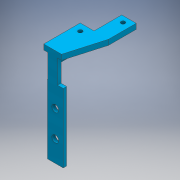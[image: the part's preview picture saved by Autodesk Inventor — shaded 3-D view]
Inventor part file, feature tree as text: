
AUTODESK INVENTOR PART (.ipt)
format: ipt  version: 2018.3 (Build 223284000, 284)  size: 1,038,848 bytes
history: native  units: mm
features: extrude x95, sketch x95, other x2
ambient origin geometry x8: Origin, YZ Plane, XZ Plane, XY Plane, X Axis, Y Axis, Z Axis, Center Point
bodies: Body1 (feature_tree), Body2 (feature_tree)
feature tree (192):
  other  "Sólido1"
  extrude  "Extrusión1"  Depth=10.0mm TaperAngle=0.0deg
  extrude  "Extrusión2"  Depth=33.0mm TaperAngle=0.0deg
  extrude  "Extrusión3"  Depth=29.0mm TaperAngle=0.0deg
  extrude  "Extrusión4"  Depth=21.0mm
  extrude  "Extrusión5"  Depth=4.0mm TaperAngle=0.0deg
  extrude  "Extrusión6"  Depth=37.0mm TaperAngle=0.0deg
  extrude  "Extrusión7"  Depth=94.0mm TaperAngle=0.0deg
  extrude  "Extrusión8"  Depth=15.0mm
  extrude  "Extrusión9"  Depth=64.0mm TaperAngle=0.0deg
  extrude  "Extrusión10"  Depth=10.0mm
  extrude  "Extrusión11"  Depth=64.0mm TaperAngle=0.0deg
  extrude  "Extrusión13"  Depth=10.0mm
  extrude  "Extrusión14"  Depth=10.0mm
  extrude  "Extrusión15"  Depth=19.0mm TaperAngle=0.0deg
  extrude  "Extrusión17"  Depth=19.0mm TaperAngle=0.0deg
  extrude  "Extrusión18"  Depth=15.0mm TaperAngle=0.0deg
  extrude  "Extrusión19"  Depth=3.0mm
  extrude  "Extrusión20"  Depth=6.0mm TaperAngle=0.0deg
  extrude  "Extrusión21"  Depth=10.0mm TaperAngle=0.0deg
  extrude  "Extrusión22"  Depth=10.0mm TaperAngle=0.0deg
  extrude  "Extrusión23"  Depth=10.0mm TaperAngle=0.0deg
  extrude  "Extrusión27"  Depth=15.0mm
  extrude  "Extrusión28"  Depth=5.0mm
  extrude  "Extrusión29"  Depth=4.0mm TaperAngle=0.0deg
  extrude  "Extrusión30"  Depth=24.5mm TaperAngle=0.0deg
  extrude  "Extrusión31"  Depth=24.5mm TaperAngle=0.0deg
  extrude  "Extrusión32"  Depth=4.3mm
  extrude  "Extrusión33"  Depth=3.7mm
  sketch  "Boceto34"  dims[d152=3.7mm d153=3.7mm]
  extrude  "Extrusión35"  Depth=3.7mm
  extrude  "Extrusión36"  Depth=25.5mm TaperAngle=0.0deg
  extrude  "Extrusión38"  Depth=5.2mm
  extrude  "Extrusión39"  Depth=5.2mm
  extrude  "Extrusión40"  Depth=45.25mm TaperAngle=0.0deg
  extrude  "Extrusión41"  Depth=71.0mm TaperAngle=0.0deg
  extrude  "Extrusión42"  Depth=1.7mm TaperAngle=0.0deg
  extrude  "Extrusión43"  Depth=33.0mm
  extrude  "Extrusión44"  Depth=2.4mm TaperAngle=0.0deg
  extrude  "Extrusión45"  Depth=85.9mm TaperAngle=0.0deg
  extrude  "Extrusión46"  Depth=2.973mm
  extrude  "Extrusión47"  Depth=3.7mm
  extrude  "Extrusión48"  Depth=3.7mm
  extrude  "Extrusión49"  Depth=5.0mm TaperAngle=0.0deg
  extrude  "Extrusión50"  Depth=0.534mm
  extrude  "Extrusión53"  Depth=2.384mm TaperAngle=0.0deg
  extrude  "Extrusión54"  Depth=5.884mm TaperAngle=0.0deg
  extrude  "Extrusión55"  Depth=14.25mm TaperAngle=0.0deg
  extrude  "Extrusión56"  Depth=11.0mm TaperAngle=0.0deg
  extrude  "Extrusión57"  Depth=3.1mm
  sketch  "Boceto57"  dims[d235=11.0mm d236=0.0mm d237=11.0mm]
  extrude  "Extrusión58"  Depth=11.0mm
  extrude  "Extrusión59"  Depth=11.0mm TaperAngle=0.0deg
  extrude  "Extrusión60"  Depth=13.0mm TaperAngle=0.0deg
  extrude  "Extrusión61"  Depth=14.0mm TaperAngle=0.0deg
  extrude  "Extrusión62"  Depth=4.3mm
  extrude  "Extrusión63"  Depth=5.0mm TaperAngle=0.0deg
  extrude  "Extrusión64"  Depth=21.5mm TaperAngle=0.0deg
  extrude  "Extrusión65"  Depth=8.0mm TaperAngle=0.0deg
  extrude  "Extrusión66"  Depth=8.0mm TaperAngle=0.0deg
  extrude  "Extrusión67"  Depth=4.0mm TaperAngle=0.0deg
  extrude  "Extrusión68"  Depth=8.0mm TaperAngle=0.0deg
  extrude  "Extrusión69"  Depth=4.0mm TaperAngle=0.0deg
  extrude  "Extrusión74"  Depth=4.3mm TaperAngle=0.0deg
  extrude  "Extrusión75"  Depth=15.0mm TaperAngle=0.0deg
  extrude  "Extrusión76"  Depth=15.0mm TaperAngle=0.0deg
  extrude  "Extrusión77"  Depth=15.0mm TaperAngle=0.0deg
  extrude  "Extrusión78"  Depth=79.25mm TaperAngle=0.0deg
  extrude  "Extrusión79"  Depth=5.0mm TaperAngle=0.0deg
  extrude  "Extrusión80"  Depth=4.0mm TaperAngle=0.0deg
  extrude  "Extrusión81"  Depth=3.0mm
  extrude  "Extrusión82"  Depth=2.53mm TaperAngle=0.0deg
  extrude  "Extrusión83"  Depth=4.0mm TaperAngle=0.0deg
  extrude  "Extrusión84"  Depth=2.6mm TaperAngle=0.0deg
  extrude  "Extrusión85"  Depth=5.2mm TaperAngle=0.0deg
  extrude  "Extrusión86"  Depth=46.25mm TaperAngle=0.0deg
  extrude  "Extrusión87"  [1 undecoded]
  extrude  "Extrusión88"  [1 undecoded]
  extrude  "Extrusión89"  [1 undecoded]
  extrude  "Extrusión90"  [1 undecoded]
  extrude  "Extrusión91"  [1 undecoded]
  extrude  "Extrusión92"  [1 undecoded]
  extrude  "Extrusión93"  [1 undecoded]
  extrude  "Extrusión94"  [1 undecoded]
  extrude  "Extrusión95"  [1 undecoded]
  extrude  "Extrusión96"  [1 undecoded]
  extrude  "Extrusión97"  [1 undecoded]
  extrude  "Extrusión98"  [1 undecoded]
  extrude  "Extrusión99"  [1 undecoded]
  extrude  "Extrusión100"  [1 undecoded]
  extrude  "Extrusión101"  [1 undecoded]
  extrude  "Extrusión102"  [1 undecoded]
  extrude  "Extrusión103"  [1 undecoded]
  extrude  "Extrusión104"  [1 undecoded]
  extrude  "Extrusión105"  [1 undecoded]
  extrude  "Extrusión106"  [1 undecoded]
  extrude  "Extrusión107"  [1 undecoded]
  extrude  "Extrusión108"  [1 undecoded]
  sketch  "Boceto1"  dims[d0=18.0mm d1=0.0mm d2=10.0mm d3=0.0mm]
  sketch  "Boceto2"  dims[d6=3.0mm d7=33.0mm d8=0.0mm]
  sketch  "Boceto4"  dims[d9=35.0mm d10=29.0mm d11=0.0mm]
  sketch  "Boceto5"  dims[d12=2.0mm d13=21.0mm]
  sketch  "Boceto6"  dims[d14=20.0mm d15=4.0mm d16=0.0mm]
  sketch  "Boceto7"  dims[d17=8.0mm d18=0.0mm d19=37.0mm d20=0.0mm]
  sketch  "Boceto8"  dims[d21=2.0mm d22=94.0mm d23=0.0mm]
  sketch  "Boceto9"  dims[d30=5.0mm d31=15.0mm]
  sketch  "Boceto12"  dims[d32=15.0mm d33=64.0mm d34=0.0mm]
  sketch  "Boceto13"  dims[d35=64.0mm d36=0.0mm d38=10.0mm]
  sketch  "Boceto15"  dims[d40=15.0mm d41=64.0mm d42=0.0mm]
  sketch  "Boceto17"  dims[d48=46.25mm d49=10.0mm]
  sketch  "Boceto18"  dims[d50=23.0mm d51=0.0mm d52=10.0mm]
  sketch  "Boceto19"  dims[d53=19.0mm d54=0.0mm d58=19.0mm d59=0.0mm]
  sketch  "Boceto20"  dims[d68=19.0mm d69=0.0mm d70=19.0mm d71=0.0mm]
  sketch  "Boceto21"  dims[d73=19.0mm d74=0.0mm d76=15.0mm d77=0.0mm]
  sketch  "Boceto22"  dims[d78=4.0mm d79=0.0mm d80=3.0mm]
  sketch  "Boceto23"  dims[d81=6.0mm d82=0.0mm d87=6.0mm d88=0.0mm]
  sketch  "Boceto24"  dims[d89=4.0mm d96=10.0mm d97=0.0mm]
  sketch  "Boceto25"  dims[d101=10.0mm d102=0.0mm d104=10.0mm d105=0.0mm]
  sketch  "Boceto26"  dims[d106=2.0mm d107=10.0mm d108=0.0mm]
  sketch  "Boceto27"  dims[d110=11.0mm d111=15.0mm]
  sketch  "Boceto28"  dims[d112=10.0mm d113=0.0mm d114=5.0mm]
  sketch  "Boceto29"  dims[d115=23.0mm d116=0.0mm d117=4.0mm d118=0.0mm]
  sketch  "Boceto30"  dims[d124=24.5mm d125=0.0mm d132=24.5mm d133=0.0mm]
  sketch  "Boceto31"  dims[d141=24.5mm d142=0.0mm d145=24.5mm d146=0.0mm]
  sketch  "Boceto32"  dims[d147=10.0mm d148=0.0mm d149=4.3mm]
  sketch  "Boceto33"  dims[d150=4.3mm d151=3.7mm]
  sketch  "Boceto35"  dims[d154=3.7mm d155=25.5mm d156=0.0mm]
  sketch  "Boceto37"  dims[d157=5.2mm d158=5.2mm]
  sketch  "Boceto38"  dims[d159=25.5mm d160=0.0mm d161=5.2mm]
  sketch  "Boceto39"  dims[d162=5.2mm d163=45.25mm d164=0.0mm]
  sketch  "Boceto40"  dims[d165=2.6mm d166=71.0mm d167=0.0mm]
  sketch  "Boceto41"  dims[d168=10.005mm d169=1.7mm d170=0.0mm]
  sketch  "Boceto42"  dims[d171=33.0mm d172=33.0mm]
  sketch  "Boceto43"  dims[d173=38.28mm d174=4.0mm d175=0.0mm d176=0.0mm d178=2.4mm d179=0.0mm]
  sketch  "Boceto44"  dims[d180=6.15mm d181=0.0mm d184=85.9mm d185=0.0mm]
  sketch  "Boceto45"  dims[d186=2.973mm d187=2.973mm]
  sketch  "Boceto46"  dims[d188=5.0mm d189=0.0mm d205=3.7mm]
  sketch  "Boceto47"  dims[d209=3.7mm d210=3.7mm]
  sketch  "Boceto48"  dims[d211=3.7mm d212=5.0mm d213=0.0mm]
  sketch  "Boceto49"  dims[d214=5.0mm d215=0.0mm d216=0.534mm]
  sketch  "Boceto50"  dims[d217=5.0mm d218=0.0mm d219=2.384mm d220=0.0mm]
  sketch  "Boceto53"  dims[d221=17.6mm d222=5.884mm d223=0.0mm]
  sketch  "Boceto54"  dims[d224=3.25mm d225=14.25mm d226=0.0mm]
  sketch  "Boceto55"  dims[d227=11.0mm d228=0.0mm d229=11.0mm d230=0.0mm]
  sketch  "Boceto56"  dims[d233=3.1mm d234=3.1mm]
  sketch  "Boceto58"  dims[d238=11.0mm d239=11.0mm d240=0.0mm]
  sketch  "Boceto59"  dims[d241=11.0mm d242=0.0mm d243=13.0mm d244=0.0mm]
  sketch  "Boceto60"  dims[d245=23.0mm d246=0.0mm d247=14.0mm d248=0.0mm]
  sketch  "Boceto61"  dims[d249=15.0mm d250=0.0mm d251=4.3mm]
  sketch  "Boceto62"  dims[d252=8.0mm d253=0.0mm d254=5.0mm d255=0.0mm]
  sketch  "Boceto63"  dims[d268=1.0mm d269=21.5mm d270=0.0mm]
  sketch  "Boceto64"  dims[d271=0.389mm d272=8.0mm d273=0.0mm]
  sketch  "Boceto65"  dims[d276=8.0mm d277=0.0mm d279=8.0mm d280=0.0mm]
  sketch  "Boceto66"  dims[d282=8.0mm d283=0.0mm d285=4.0mm d286=0.0mm]
  sketch  "Boceto67"  dims[d288=4.0mm d289=0.0mm d291=8.0mm d292=0.0mm]
  sketch  "Boceto70"  dims[d293=0.135mm d294=4.0mm d295=0.0mm]
  sketch  "Boceto75"  dims[d296=4.3mm d297=0.0mm d299=4.3mm d300=0.0mm]
  sketch  "Boceto76"  dims[d303=15.0mm d304=0.0mm d306=15.0mm d307=0.0mm]
  sketch  "Boceto77"  dims[d309=15.0mm d310=0.0mm d311=15.0mm d312=0.0mm]
  sketch  "Boceto78"  dims[d314=15.0mm d315=0.0mm d316=15.0mm d317=0.0mm]
  sketch  "Boceto79"  dims[d318=1.17mm d319=0.0mm d320=79.25mm d321=0.0mm]
  sketch  "Boceto80"  dims[d334=5.0mm d335=0.0mm d336=5.0mm d337=0.0mm]
  sketch  "Boceto81"  dims[d338=0.03mm d339=0.0mm d340=4.0mm d341=0.0mm]
  sketch  "Boceto82"  dims[d342=4.0mm d343=0.0mm d344=3.0mm]
  sketch  "Boceto83"  dims[d345=4.0mm d346=0.0mm d347=2.53mm d348=0.0mm]
  sketch  "Boceto84"  dims[d349=4.0mm d350=0.0mm d352=4.0mm d353=0.0mm]
  sketch  "Boceto86"  dims[d354=5.0mm d355=0.0mm d356=2.6mm d357=0.0mm]
  sketch  "Boceto87"  dims[d361=5.2mm d362=0.0mm d365=5.2mm d366=0.0mm]
  sketch  "Boceto88"  dims[d367=46.25mm d368=0.0mm d369=46.25mm d370=0.0mm]
  sketch  "Boceto89"  dims[d371=2.6mm d372=0.0mm]
  sketch  "Boceto90"
  sketch  "Boceto91"
  sketch  "Boceto92"
  sketch  "Boceto93"
  sketch  "Boceto94"
  sketch  "Boceto95"
  sketch  "Boceto96"
  sketch  "Boceto97"
  sketch  "Boceto99"
  sketch  "Boceto100"
  sketch  "Boceto101"
  sketch  "Boceto102"
  sketch  "Boceto103"
  sketch  "Boceto104"
  sketch  "Boceto105"
  sketch  "Boceto106"
  sketch  "Boceto107"
  sketch  "Boceto108"
  sketch  "Boceto111"
  sketch  "Boceto112"
  sketch  "Boceto113"
  other  "Saliente-Extruir7"
note: 22 required parameter values undecoded (feature->parameter linkage not recoverable at this tier; creation-order binding heuristic only, values carry confidence <= 0.55)
